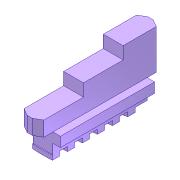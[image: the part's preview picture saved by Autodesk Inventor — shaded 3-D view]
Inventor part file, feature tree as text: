
AUTODESK INVENTOR PART (.ipt)
format: ipt  version: unknown  size: 337,408 bytes
history: native  units: in
note: dims shown in document units (in); Inventor stores cm internally (conversion verified against a paired STEP export)
features: extrude x7, sketch x7, fillet x1, projected_geometry x1
ambient origin geometry x8: Origin, YZ Plane, XZ Plane, XY Plane, X Axis, Y Axis, Z Axis, Center Point
feature tree (16):
  extrude  "Extrusion8"  Depth=0.1378in
  extrude  "Extrusion9"  Depth=0.0787in
  extrude  "Extrusion10"  Depth=0.315in
  extrude  "Extrusion11"  TaperAngle=30.0deg  [1 undecoded]
  extrude  "Extrusion13"  Depth=0.7874in TaperAngle=0.0deg
  extrude  "Extrusion14"  Depth=0.1969in TaperAngle=0.0deg
  fillet  "Fillet1"  Radius=0.315in
  extrude  "Extrusion16"  Depth=0.1181in
  sketch  "Sketch10"  dims[d51=0.0787in d52=0.1378in]
  sketch  "Sketch11"  dims[d53=0.0787in d54=0.0787in]
  sketch  "Sketch12"  dims[d55=0.0787in d56=0.315in]
  sketch  "Sketch13"  dims[d57=0.9843in d58=0.0in d59=30.0deg]
  sketch  "Sketch15"  dims[d60=30.0deg d61=0.7874in d62=0.0in]
  sketch  "Sketch16"  dims[d63=0.315in d64=0.1969in d65=0.0in d66=0.315in]
  sketch  "Sketch18"  dims[d67=0.0984in d68=0.0in d72=0.1181in d73=0.1181in d74=0.0787in d75=0.0in d76=0.4567in d79=0.0551in d81=0.0551in d83=0.0551in d85=0.0551in d87=0.0551in d89=0.0551in d90=0.0354in d91=0.0in d92=0.1181in d93=0.1181in d94=0.1181in d95=0.1181in d96=0.1181in d102=0.0008in d103=0.0118in d104=0.0118in d105=0.3937in d106=0.0in]
  projected_geometry  "Projected Loop1"
note: 1 required parameter value undecoded (feature->parameter linkage not recoverable at this tier; creation-order binding heuristic only, values carry confidence <= 0.55)
